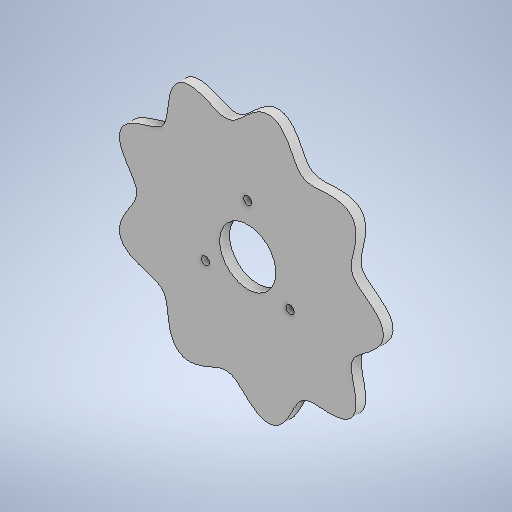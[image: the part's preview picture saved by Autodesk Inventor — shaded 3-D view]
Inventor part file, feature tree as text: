
AUTODESK INVENTOR PART (.ipt)
format: ipt  version: 2025 (Build 290162000, 162)  size: 433,664 bytes
history: native  units: mm
features: sketch x5, extrude x4, other x1
ambient origin geometry x8: Origin, YZ Plane, XZ Plane, XY Plane, X Axis, Y Axis, Z Axis, Center Point
bodies: 实体1 (feature_tree)
feature tree (10):
  sketch  "草图1"  dims[d0=67.5mm d1=40.0mm]
  extrude  "拉伸1"  Depth=40.0mm
  extrude  "拉伸2"  Depth=30.0mm TaperAngle=360.0deg
  sketch  "草图2"  dims[d7=1.0mm d10=23.0mm]
  extrude  "拉伸5"  Depth=23.0mm
  extrude  "拉伸6"  Depth=20.0mm TaperAngle=0.0deg
  sketch  "草图 - 环形阵列1"  dims[d2=3.4mm d3=30.0mm d5=360.0deg]
  sketch  "草图3"  dims[d11=4.0mm d12=0.0mm d13=20.0mm d14=0.0mm]
  sketch  "草图 - 环形阵列3"  dims[d20=84.5mm d21=67.0mm d22=90.0mm d23=97.0mm d24=85.1mm d25=1.0mm d41=30.0mm d42=0.0mm d43=3.15mm d44=90.0mm d46=360.0deg d48=8.0mm d49=0.0mm d66=0.0mm d67=3600.0mm d68=0.5mm]
  other  "二维表达式曲线2"
